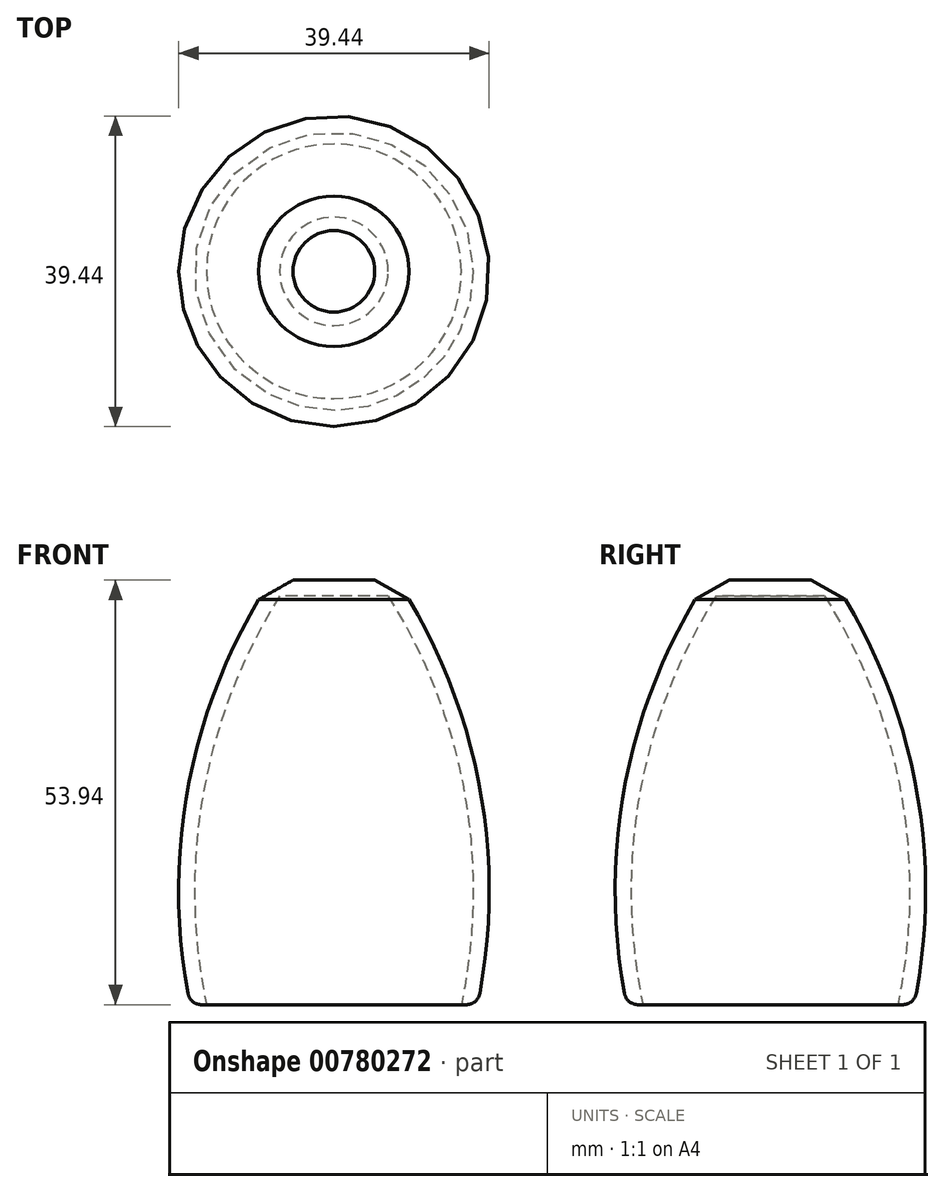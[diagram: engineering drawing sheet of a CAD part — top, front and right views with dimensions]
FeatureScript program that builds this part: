
annotation { "Feature Type Name" : "Feature", "Feature Type Description" : "" }
export const myFeature = defineFeature(function(context is Context, id is Id, definition is map)
    precondition{}
    {
        {
            var Q0;
            Q0=qCreatedBy(makeId("Front.planeOp"),FACE);
            var sketch = newSketch(context, id + "F0", { "sketchPlane" : qUnion([Q0])});
            skLineSegment(sketch, "E0", {"start": v(0, 0) * mm, "end": v(18.26, 0) * mm});
            skLineSegment(sketch, "E1", {"start": v(0, 53.94) * mm, "end": v(8, 53.94) * mm});
            skArc(sketch, "E2", {"start": v(18.26, 0) * mm, "mid": v(18.45, 27.98) * mm, "end": v(8, 53.94) * mm});
            skPoint(sketch, "E3.end.orphan", {"position": v(0, 31.07) * mm});
            skLineSegment(sketch, "E4", {"start": v(0, 53.94) * mm, "end": v(0, 0) * mm});
            skSolve(sketch);
        }
        {
            var Q0;
            Q0=makeQuery(id+"F0.imprint","IMPRINT",FACE,{"disambiguationData":[TD([[makeQuery(id+"F0.imprint","IMPRINT",EDGE,{"derivedFrom":sQuery(id+"F0.wireOp",EDGE,"E0")}),1.0]])]});
            var Q1;
            Q1=sQuery(id+"F0.wireOp",EDGE,"E4");
            revolve(context, id + "F1", {"surfaceOperationType" : NewSurfaceOperationType.NEW, "entities" : qUnion([Q0]), "axis" : qUnion([Q1]), "revolveType" : RevolveType.FULL});
        }
        {
            var Q0;
            Q0=makeQuery(id+"F1.opRevolve","SWEPT_FACE",FACE,{"disambiguationData":[OSD([sQuery(id+"F0.wireOp",EDGE,"E0")])]});
            shell(context, id + "F2", {"entities" : qUnion([Q0]), "thickness" : 2.03 * mm});
        }
        {
            var Q0;
            Q0=makeQuery(id+"F1.opRevolve","SWEPT_EDGE",EDGE,{"disambiguationData":[OSD([sQuery(id+"F0.wireOp",EDGE,"E0"),sQuery(id+"F0.wireOp",EDGE,"E2")])]});
            fillet(context, id + "F3", {"entities" : qUnion([Q0]), "radius" : 1.75 * mm, "tangentPropagation" : true, "allowEdgeOverflow" : false});
        }
        {
            var Q0;
            Q0=makeQuery(id+"F1.opRevolve","SWEPT_EDGE",EDGE,{"disambiguationData":[OSD([sQuery(id+"F0.wireOp",EDGE,"E1"),sQuery(id+"F0.wireOp",EDGE,"E2")])]});
            chamfer(context, id + "F4", {"entities" : qUnion([Q0]), "width" : 5.08 * mm, "tangentPropagation" : true});
        }
    });
